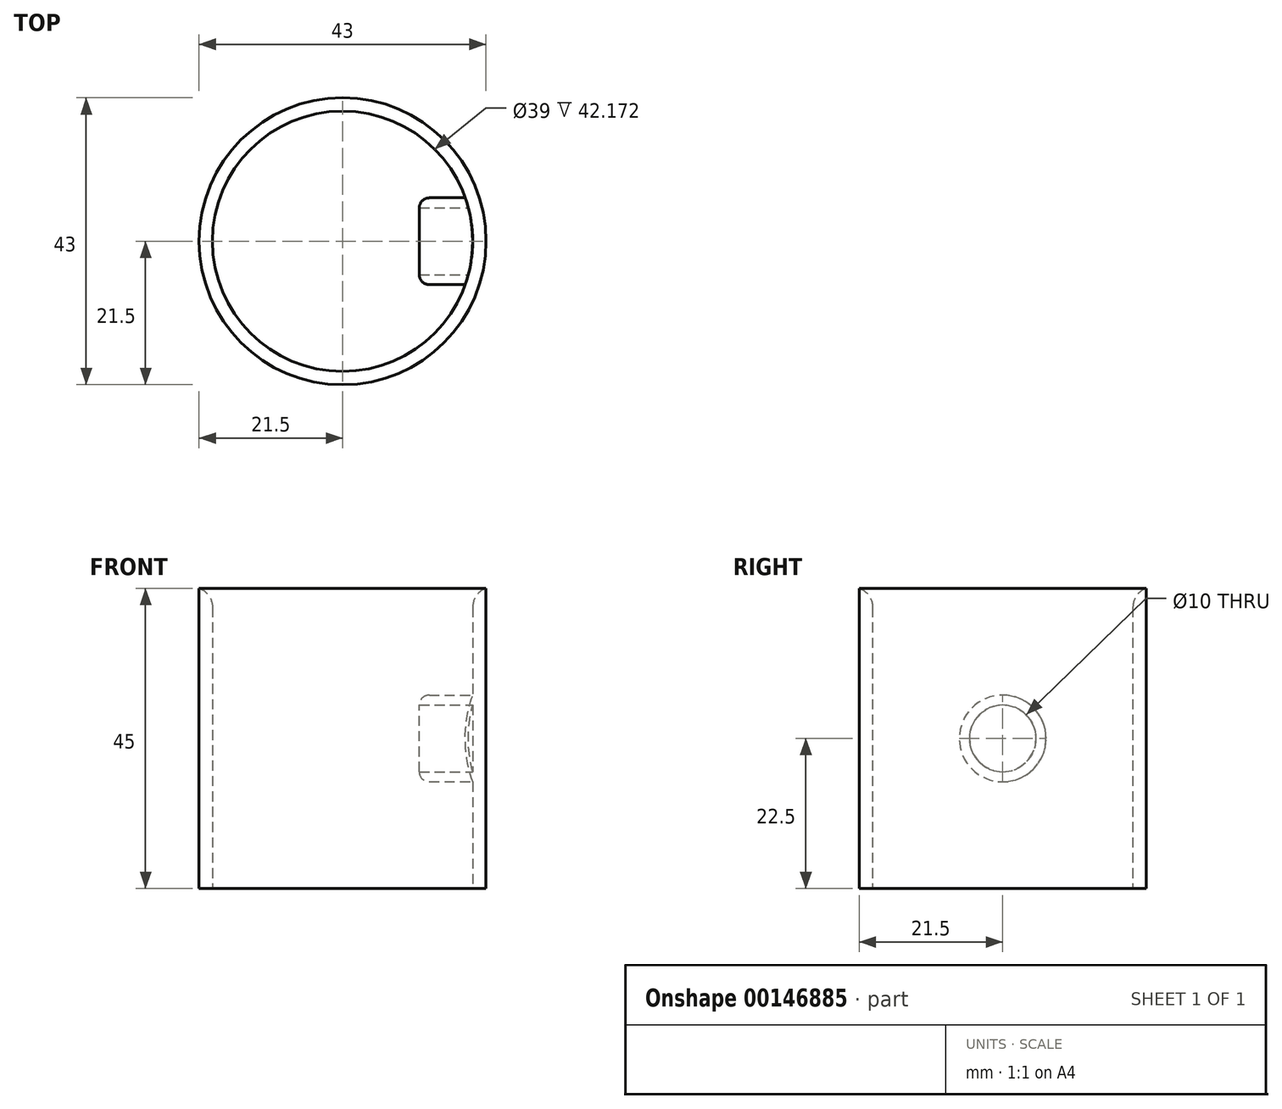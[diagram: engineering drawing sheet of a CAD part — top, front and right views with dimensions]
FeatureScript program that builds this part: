
annotation { "Feature Type Name" : "Feature", "Feature Type Description" : "" }
export const myFeature = defineFeature(function(context is Context, id is Id, definition is map)
    precondition{}
    {
        {
            var Q0;
            Q0=qCreatedBy(makeId("Top.planeOp"),FACE);
            var sketch = newSketch(context, id + "F0", { "sketchPlane" : qUnion([Q0])});
            skCircle(sketch, "E0", {"center": v(0, 0) * mm, "radius": 21.5 * mm});
            skCircle(sketch, "E1", {"center": v(0, 0) * mm, "radius": 19.5 * mm});
            skPoint(sketch, "E2", {"position": v(0, -19.5) * mm});
            skPoint(sketch, "E3", {"position": v(0, 19.5) * mm});
            skLineSegment(sketch, "E4", {"start": v(0, -21.5) * mm, "end": v(0, 21.5) * mm});
            skPoint(sketch, "E5", {"position": v(19.5, 0) * mm});
            skPoint(sketch, "E6", {"position": v(-19.5, 0) * mm});
            skSolve(sketch);
        }
        {
            var Q0;
            {var subQ0=sQuery(id+"F0.wireOp",EDGE,"E4");var subQ1=sQuery(id+"F0.wireOp",EDGE,"E0");var subQ2=makeQuery(id+"F0.imprint","INTERSECT",VERTEX,{"disambiguationData":[OD(0.0)],"derivedFrom":[subQ1,subQ0]});Q0=makeQuery(id+"F0.imprint","IMPRINT",FACE,{"disambiguationData":[TD([[makeQuery(id+"F0.imprint","IMPRINT",EDGE,{"disambiguationData":[TD([[subQ2,-1.0]])],"derivedFrom":subQ1}),1.0]])]});}
            extrude(context, id + "F1", {"entities" : qUnion([Q0]), "depth" : 45 * mm});
        }
        {
            var Q0;
            Q0=qCreatedBy(makeId("Right.planeOp"),FACE);
            var Q1;
            Q1=sQuery(id+"F0.wireOp",VERTEX,"E5");
            cPlane(context, id + "F2", {"entities" : qUnion([Q0, Q1]), "cplaneType" : CPlaneType.PLANE_POINT, "offset" : 25 * mm, "width" : 150 * mm, "height" : 150 * mm});
        }
        {
            var Q0;
            Q0=qCreatedBy(id+"F2.planeOp",FACE);
            var sketch = newSketch(context, id + "F3", { "sketchPlane" : qUnion([Q0])});
            skPoint(sketch, "E7", {"position": v(0, 22.5) * mm});
            skCircle(sketch, "E8", {"center": v(0, 22.5) * mm, "radius": 5 * mm});
            skCircle(sketch, "E9", {"center": v(0, 22.5) * mm, "radius": 6.5 * mm});
            skSolve(sketch);
        }
        {
            var Q0;
            Q0 = qSketchRegion(id + "F3", true);
            extrude(context, id + "F4", {"entities" : qUnion([Q0]), "operationType" : NewBodyOperationType.ADD, "oppositeDirection" : true, "depth" : 8 * mm});
        }
        {
            var Q0;
            Q0=makeQuery(id+"F3.imprint","IMPRINT",FACE,{"disambiguationData":[TD([[makeQuery(id+"F3.imprint","IMPRINT",EDGE,{"derivedFrom":sQuery(id+"F3.wireOp",EDGE,"E8")}),1.0]])]});
            extrude(context, id + "F5", {"entities" : qUnion([Q0]), "operationType" : NewBodyOperationType.REMOVE, "depth" : 1 * mm});
        }
        {
            var Q0;
            Q0=makeQuery(id+"F1.opExtrude","SWEPT_BODY",BODY,{"disambiguationData":[OSD([sQuery(id+"F0.wireOp",EDGE,"E0"),sQuery(id+"F0.wireOp",EDGE,"E1"),sQuery(id+"F0.wireOp",EDGE,"E4")])]});
            var Q1;
            Q1=qCreatedBy(makeId("Right.planeOp"),FACE);
            mirror(context, id + "F6", {"operationType" : NewBodyOperationType.ADD, "entities" : qUnion([Q0]), "mirrorPlane" : qUnion([Q1])});
        }
        {
            var Q0;
            {var subQ0=makeQuery(id+"F1.opExtrude","CAP_EDGE",EDGE,{"disambiguationData":[OSD([sQuery(id+"F0.wireOp",EDGE,"E1")])],"isStart":false});Q0=makeQuery(id+"F6.boolean.opBoolean","MERGE",EDGE,{"derivedFrom":[subQ0,makeQuery(id+"F6.opPattern","COPY",EDGE,{"derivedFrom":subQ0,"instanceName":"1"})]});}
            fillet(context, id + "F7", {"entities" : qUnion([Q0]), "radius" : 3 * mm, "tangentPropagation" : true, "allowEdgeOverflow" : false});
        }
        {
            var Q0;
            Q0=makeQuery(id+"F4.opExtrude","CAP_EDGE",EDGE,{"disambiguationData":[OSD([sQuery(id+"F3.wireOp",EDGE,"E9")])],"isStart":false});
            var Q1;
            Q1=makeQuery(id+"F6.opPattern","COPY",EDGE,{"derivedFrom":makeQuery(id+"F4.opExtrude","CAP_EDGE",EDGE,{"disambiguationData":[OSD([sQuery(id+"F3.wireOp",EDGE,"E9")])],"isStart":false}),"instanceName":"1"});
            fillet(context, id + "F8", {"entities" : qUnion([Q0, Q1]), "radius" : 1.5 * mm, "tangentPropagation" : true, "allowEdgeOverflow" : false});
        }
    });
